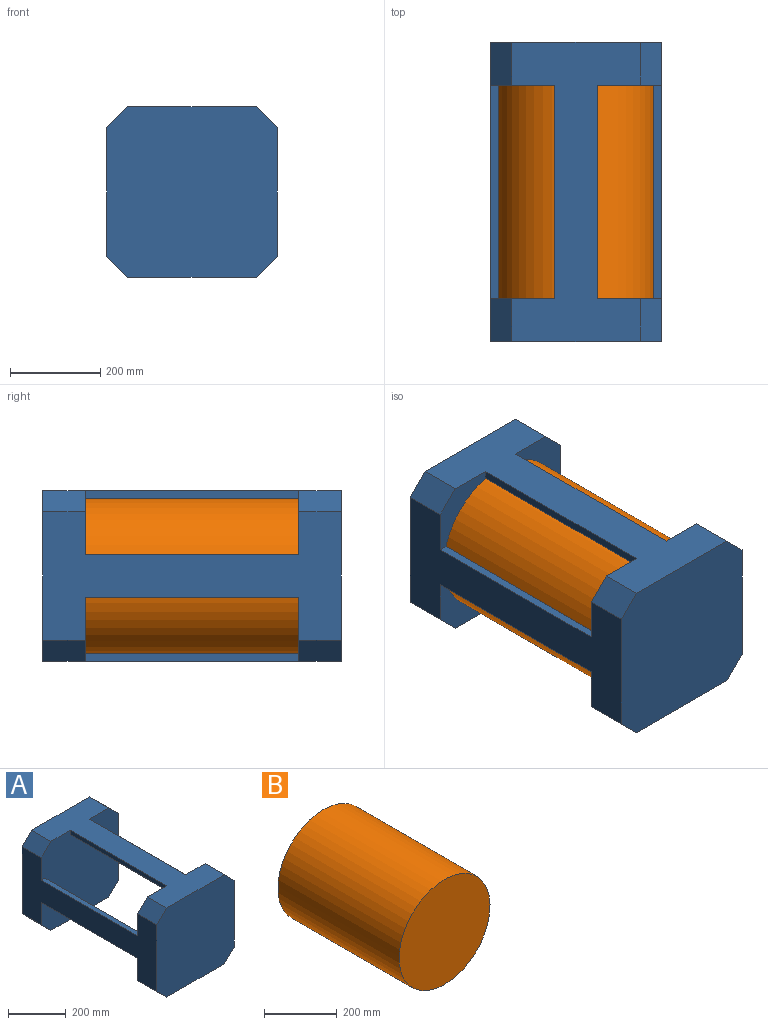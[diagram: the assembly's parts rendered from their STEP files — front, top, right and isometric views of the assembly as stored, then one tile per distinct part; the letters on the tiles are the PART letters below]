
ASSEMBLY  parts=2 mates=1
PART A: 28 faces, bbox 377.4x660.4x377.4 mm
  f0: plane 377.37x377.37mm, normal (0,1,0), area 132708.8mm2, adj f1,f2,f3,f4,f5,f6,f7,f8
  f1: plane 660.4x283.03mm, normal (0,0,-1), area 97906.3mm2, adj f0,f2,f8,f9,f13,f14,f22,f23
  f2: plane 94.34x47.17mm, normal (0.71,0,-0.71), area 6293.7mm2, adj f0,f1,f3,f9
  f3: plane 660.4x283.03mm, normal (1,0,0), area 97906.3mm2, adj f0,f2,f4,f9,f19,f21,f22,f23
  f4: plane 94.34x47.17mm, normal (0.71,0,0.71), area 6293.7mm2, adj f0,f3,f5,f9
  f5: plane 660.4x283.03mm, normal (0,0,1), area 97906.3mm2, adj f0,f4,f6,f9,f10,f12,f22,f24
  f6: plane 94.34x47.17mm, normal (-0.71,0,0.71), area 6293.7mm2, adj f0,f5,f7,f9
  f7: plane 660.4x283.03mm, normal (-1,0,0), area 97906.3mm2, adj f0,f6,f8,f9,f17,f18,f22,f25
  f8: plane 94.34x47.17mm, normal (-0.71,0,-0.71), area 6293.7mm2, adj f0,f1,f7,f9
  f9: plane 377.37x377.37mm, normal (0,-1,0), area 137958.9mm2, adj f1,f2,f3,f4,f5,f6,f7,f8
  f10: plane 471.71x18.2mm, normal (-1,0,0), area 8584.4mm2, adj f0,f5,f11,f22
  f11: cylinder r=176.89mm len=471.71mm, axis (0,-1,0), area 45047.9mm2, adj f0,f10,f12,f22
  f12: plane 471.71x18.2mm, normal (1,0,0), area 8584.4mm2, adj f0,f5,f11,f22
  f13: plane 471.71x18.2mm, normal (-1,0,0), area 8584.4mm2, adj f0,f1,f15,f22
  f14: plane 471.71x18.2mm, normal (1,0,0), area 8584.4mm2, adj f0,f1,f15,f22
  f15: cylinder r=176.89mm len=471.71mm, axis (0,-1,0), area 45047.9mm2, adj f0,f13,f14,f22
  f16: cylinder r=176.89mm len=471.71mm, axis (0,-1,0), area 45047.9mm2, adj f0,f17,f18,f22
  f17: plane 471.71x18.2mm, normal (0,0,1), area 8584.4mm2, adj f0,f7,f16,f22
  f18: plane 471.71x18.2mm, normal (0,0,-1), area 8584.4mm2, adj f0,f7,f16,f22
  f19: plane 471.71x18.2mm, normal (0,0,1), area 8584.4mm2, adj f0,f3,f20,f22
  f20: cylinder r=176.89mm len=471.71mm, axis (0,-1,0), area 45047.9mm2, adj f0,f19,f21,f22
  f21: plane 471.71x18.2mm, normal (0,0,-1), area 8584.4mm2, adj f0,f3,f20,f22
  f22: plane 377.37x377.37mm, normal (0,-1,0), area 132708.8mm2, adj f1,f3,f5,f7,f10,f11,f12,f13
  f23: plane 94.34x47.17mm, normal (0.71,0,-0.71), area 6293.7mm2, adj f1,f3,f22,f27
  f24: plane 94.34x47.17mm, normal (0.71,0,0.71), area 6293.7mm2, adj f3,f5,f22,f27
  f25: plane 94.34x47.17mm, normal (-0.71,0,0.71), area 6293.7mm2, adj f5,f7,f22,f27
  f26: plane 94.34x47.17mm, normal (-0.71,0,-0.71), area 6293.7mm2, adj f1,f7,f22,f27
  f27: plane 377.37x377.37mm, normal (0,1,0), area 137958.9mm2, adj f1,f3,f5,f7,f23,f24,f25,f26
PART B: 3 faces, bbox 353.8x471.7x353.8 mm
  f0: cylinder r=176.89mm len=471.71mm, axis (0,-1,0), area 524287.1mm2, adj f1,f2
  f1: plane 353.79x353.79mm, normal (0,1,0), area 98303.8mm2, adj f0
  f2: plane 353.79x353.79mm, normal (0,-1,0), area 98303.8mm2, adj f0
PLACE A t=(3.39,-1015.24,-1.8)mm
PLACE B t=(470.75,-1015.24,-1.8)mm
MATE fastened B.f0 <-> A.f20  axis (0,-1,0) through (3.39,218.47,-1.8)mm
